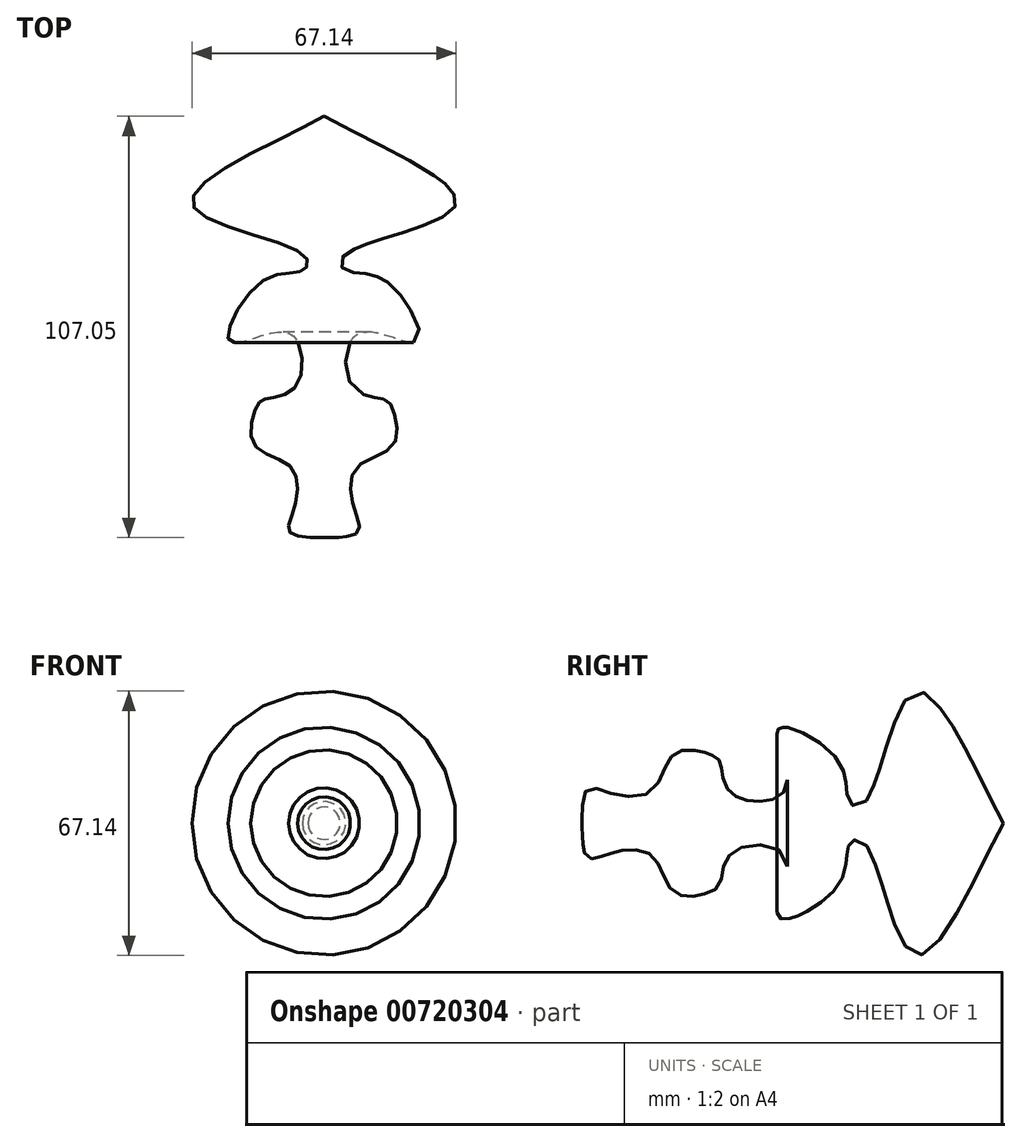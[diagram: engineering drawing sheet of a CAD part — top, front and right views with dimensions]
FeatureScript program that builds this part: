
annotation { "Feature Type Name" : "Feature", "Feature Type Description" : "" }
export const myFeature = defineFeature(function(context is Context, id is Id, definition is map)
    precondition{}
    {
        {
            var Q0;
            Q0=qCreatedBy(makeId("Top.planeOp"),FACE);
            var sketch = newSketch(context, id + "F0", { "sketchPlane" : qUnion([Q0])});
            skFitSpline(sketch, "E0", {"points": [v(0, 41.8) * mm, v(-33.5, 19.53) * mm, v(-5.1, 6.48) * mm, v(-5.37, 2.62) * mm, v(-15.58, 0) * mm, v(-23.88, -15.41) * mm, v(-8.96, -13.38) * mm, v(-7.03, -26.62) * mm, v(-14.48, -29.93) * mm, v(-16.96, -31.6) * mm, v(-17.79, -41.52) * mm, v(-8.4, -47.32) * mm, v(-7.58, -57.8) * mm, v(-8.69, -63.87) * mm, v(0, -65.25) * mm], "startDerivative": vector(-218.67, -128.82) * mm, "endDerivative": vector(170.2, 0.58) * mm});
            skLineSegment(sketch, "E1", {"start": v(0, 41.8) * mm, "end": v(0, -65.25) * mm, "construction": true});
            skLineSegment(sketch, "E2", {"start": v(0, 41.8) * mm, "end": v(0, -65.25) * mm});
            skSolve(sketch);
        }
        {
            var Q0;
            Q0=makeQuery(id+"F0.imprint","IMPRINT",FACE,{"disambiguationData":[TD([[makeQuery(id+"F0.imprint","IMPRINT",EDGE,{"derivedFrom":sQuery(id+"F0.wireOp",EDGE,"E0")}),1.0]])]});
            var Q1;
            Q1=sQuery(id+"F0.wireOp",EDGE,"E2");
            revolve(context, id + "F1", {"surfaceOperationType" : NewSurfaceOperationType.NEW, "entities" : qUnion([Q0]), "axis" : qUnion([Q1]), "revolveType" : RevolveType.FULL});
        }
    });
